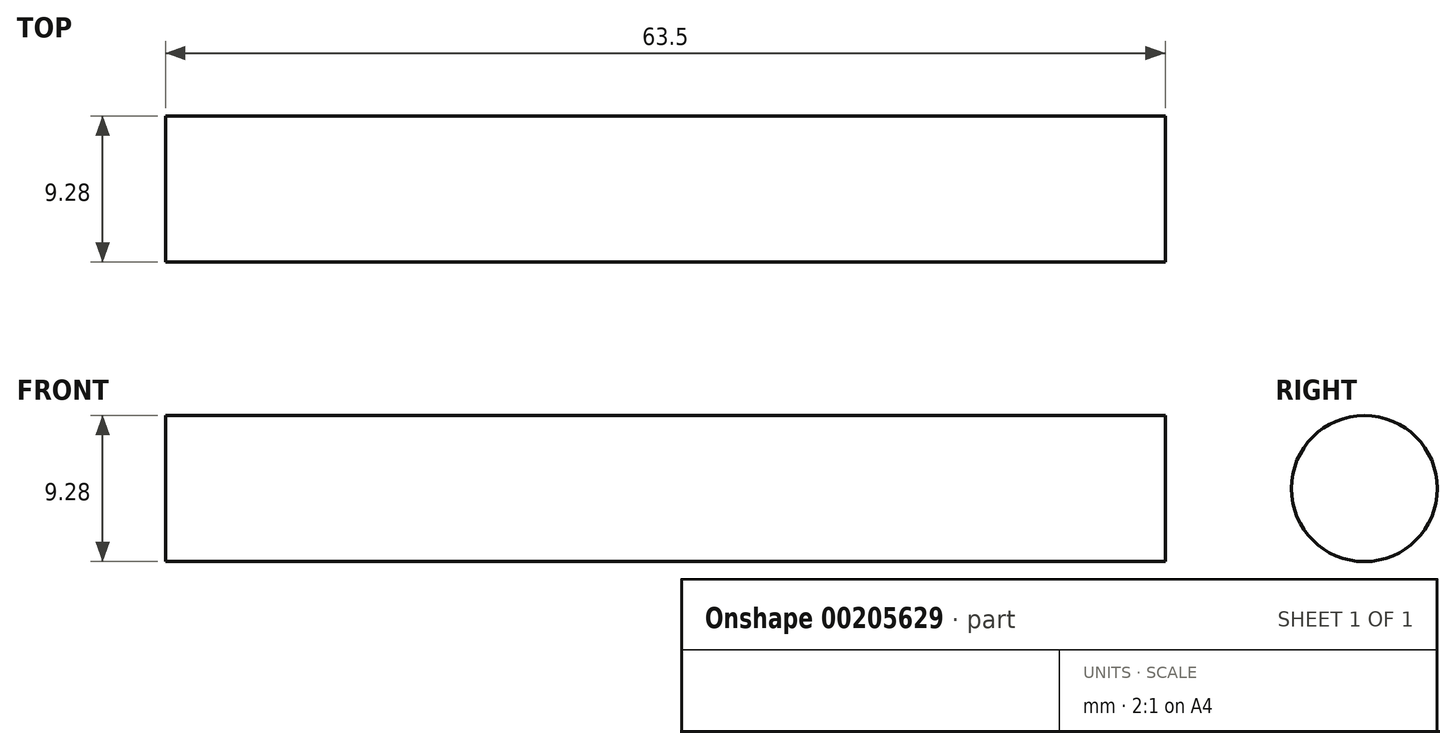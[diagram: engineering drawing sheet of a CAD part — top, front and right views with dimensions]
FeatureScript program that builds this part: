
annotation { "Feature Type Name" : "Feature", "Feature Type Description" : "" }
export const myFeature = defineFeature(function(context is Context, id is Id, definition is map)
    precondition{}
    {
        {
            var Q0;
            Q0=qCreatedBy(makeId("Right.planeOp"),FACE);
            var sketch = newSketch(context, id + "F0", { "sketchPlane" : qUnion([Q0])});
            skCircle(sketch, "E0", {"center": v(0, 0) * mm, "radius": 4.64 * mm});
            skSolve(sketch);
        }
        {
            var Q0;
            Q0=sQuery(id+"F0.wireOp",EDGE,"E0");
            extrude(context, id + "F1", {"bodyType" : ToolBodyType.SURFACE, "surfaceEntities" : qUnion([Q0]), "oppositeDirection" : true, "depth" : 63.5 * mm});
        }
        {
            var Q0;
            Q0=makeQuery(id+"F0.imprint","IMPRINT",FACE,{"disambiguationData":[TD([[makeQuery(id+"F0.imprint","IMPRINT",EDGE,{"derivedFrom":sQuery(id+"F0.wireOp",EDGE,"E0")}),1.0]])]});
            extrude(context, id + "F2", {"entities" : qUnion([Q0]), "depth" : 63.5 * mm});
        }
    });
